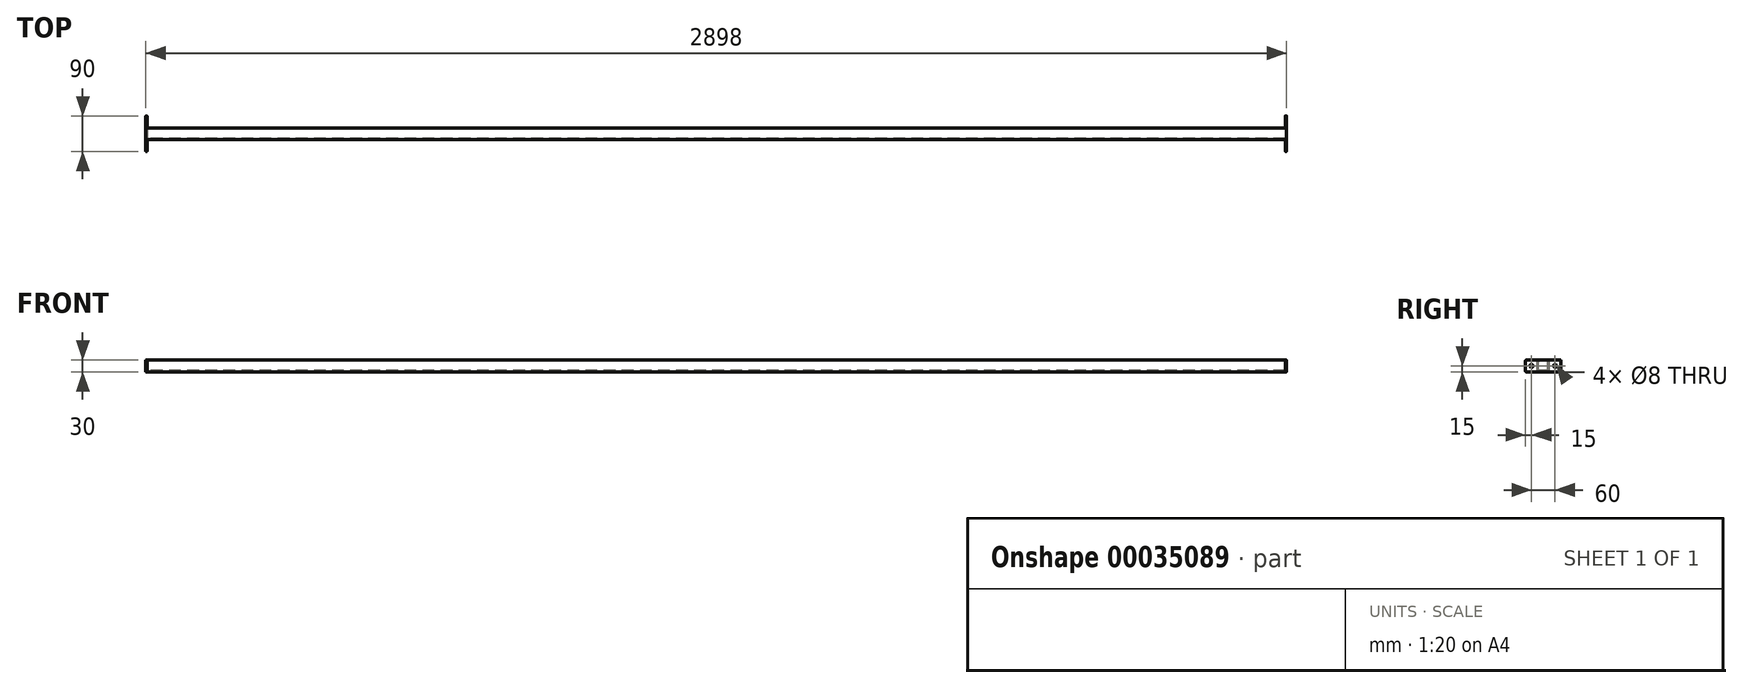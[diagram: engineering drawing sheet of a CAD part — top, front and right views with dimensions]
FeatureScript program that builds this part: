
annotation { "Feature Type Name" : "Feature", "Feature Type Description" : "" }
export const myFeature = defineFeature(function(context is Context, id is Id, definition is map)
    precondition{}
    {
        {
            var Q0;
            Q0=qCreatedBy(makeId("Right.planeOp"),FACE);
            var sketch = newSketch(context, id + "F0", { "sketchPlane" : qUnion([Q0])});
            skLineSegment(sketch, "E0.rect.bottom", {"start": v(12, -15) * mm, "end": v(-12, -15) * mm});
            skLineSegment(sketch, "E0.rect.top", {"start": v(12, 15) * mm, "end": v(-12, 15) * mm});
            skLineSegment(sketch, "E0.rect.left", {"start": v(15, -12) * mm, "end": v(15, 12) * mm});
            skLineSegment(sketch, "E0.rect.right", {"start": v(-15, -12) * mm, "end": v(-15, 12) * mm});
            skPoint(sketch, "E0.rect.middle", {"position": v(0, 0) * mm});
            skPoint(sketch, "E1.visualSharp", {"position": v(-15, 15) * mm});
            skArc(sketch, "E1.filletArc", {"start": v(-12, 15) * mm, "mid": v(-14.12, 14.12) * mm, "end": v(-15, 12) * mm});
            skPoint(sketch, "E2.visualSharp", {"position": v(15, 15) * mm});
            skArc(sketch, "E2.filletArc", {"start": v(15, 12) * mm, "mid": v(14.12, 14.12) * mm, "end": v(12, 15) * mm});
            skPoint(sketch, "E3.visualSharp", {"position": v(15, -15) * mm});
            skArc(sketch, "E3.filletArc", {"start": v(12, -15) * mm, "mid": v(14.12, -14.12) * mm, "end": v(15, -12) * mm});
            skPoint(sketch, "E4.visualSharp", {"position": v(-15, -15) * mm});
            skArc(sketch, "E4.filletArc", {"start": v(-15, -12) * mm, "mid": v(-14.12, -14.12) * mm, "end": v(-12, -15) * mm});
            skLineSegment(sketch, "E5.0", {"start": v(10, -12) * mm, "end": v(-10, -12) * mm});
            skLineSegment(sketch, "E5.1", {"start": v(12, -10) * mm, "end": v(12, 10) * mm});
            skLineSegment(sketch, "E5.2", {"start": v(10, 12) * mm, "end": v(-10, 12) * mm});
            skLineSegment(sketch, "E5.3", {"start": v(-12, -10) * mm, "end": v(-12, 10) * mm});
            skArc(sketch, "E6.filletArc", {"start": v(-10, 12) * mm, "mid": v(-11.41, 11.41) * mm, "end": v(-12, 10) * mm});
            skArc(sketch, "E7.filletArc", {"start": v(12, 10) * mm, "mid": v(11.41, 11.41) * mm, "end": v(10, 12) * mm});
            skArc(sketch, "E8.filletArc", {"start": v(10, -12) * mm, "mid": v(11.41, -11.41) * mm, "end": v(12, -10) * mm});
            skArc(sketch, "E9.filletArc", {"start": v(-12, -10) * mm, "mid": v(-11.41, -11.41) * mm, "end": v(-10, -12) * mm});
            skSolve(sketch);
        }
        {
            var Q0;
            Q0=qCreatedBy(makeId("Right.planeOp"),FACE);
            cPlane(context, id + "F1", {"entities" : qUnion([Q0]), "cplaneType" : CPlaneType.OFFSET, "offset" : 2898 * mm, "width" : 150 * mm, "height" : 150 * mm});
        }
        {
            var Q0;
            Q0=qSketchRegion(id+"F0",true);
            var Q1;
            Q1=qCreatedBy(id+"F1.planeOp",FACE);
            extrude(context, id + "F2", {"entities" : qUnion([Q0]), "endBound" : BoundingType.UP_TO_SURFACE, "endBoundEntityFace" : qUnion([Q1]), "depth" : 25 * mm});
        }
        {
            var Q0;
            Q0=qCreatedBy(makeId("Right.planeOp"),FACE);
            var sketch = newSketch(context, id + "F3", { "sketchPlane" : qUnion([Q0])});
            skLineSegment(sketch, "E10.bottom", {"start": v(43, 15) * mm, "end": v(-43, 15) * mm});
            skLineSegment(sketch, "E10.top", {"start": v(43, -15) * mm, "end": v(-43, -15) * mm});
            skLineSegment(sketch, "E10.left", {"start": v(45, 13) * mm, "end": v(45, -13) * mm});
            skLineSegment(sketch, "E10.right", {"start": v(-45, 13) * mm, "end": v(-45, -13) * mm});
            skPoint(sketch, "E11.visualSharp", {"position": v(45, 15) * mm});
            skArc(sketch, "E11.filletArc", {"start": v(45, 13) * mm, "mid": v(44.41, 14.41) * mm, "end": v(43, 15) * mm});
            skPoint(sketch, "E12.visualSharp", {"position": v(45, -15) * mm});
            skArc(sketch, "E12.filletArc", {"start": v(43, -15) * mm, "mid": v(44.41, -14.41) * mm, "end": v(45, -13) * mm});
            skPoint(sketch, "E13.visualSharp", {"position": v(-45, 15) * mm});
            skArc(sketch, "E13.filletArc", {"start": v(-43, 15) * mm, "mid": v(-44.41, 14.41) * mm, "end": v(-45, 13) * mm});
            skPoint(sketch, "E14.visualSharp", {"position": v(-45, -15) * mm});
            skArc(sketch, "E14.filletArc", {"start": v(-45, -13) * mm, "mid": v(-44.41, -14.41) * mm, "end": v(-43, -15) * mm});
            skPoint(sketch, "E15", {"position": v(30, 0) * mm});
            skPoint(sketch, "E16", {"position": v(-30, 0) * mm});
            skSolve(sketch);
        }
        {
            var Q0;
            Q0=qSketchRegion(id+"F3",true);
            extrude(context, id + "F4", {"entities" : qUnion([Q0]), "operationType" : NewBodyOperationType.ADD, "depth" : 3 * mm});
        }
        {
            var Q0;
            Q0=sQuery(id+"F3.wireOp",VERTEX,"E15");
            var Q1;
            Q1=sQuery(id+"F3.wireOp",VERTEX,"E16");
            var Q2;
            Q2=makeQuery(id+"F2.opExtrude","SWEPT_BODY",BODY,{"disambiguationData":[OSD([sQuery(id+"F0.wireOp",EDGE,"E0.rect.bottom"),sQuery(id+"F0.wireOp",EDGE,"E0.rect.top"),sQuery(id+"F0.wireOp",EDGE,"E0.rect.left"),sQuery(id+"F0.wireOp",EDGE,"E0.rect.right"),sQuery(id+"F0.wireOp",EDGE,"E1.filletArc"),sQuery(id+"F0.wireOp",EDGE,"E2.filletArc"),sQuery(id+"F0.wireOp",EDGE,"E3.filletArc"),sQuery(id+"F0.wireOp",EDGE,"E4.filletArc"),sQuery(id+"F0.wireOp",EDGE,"E5.0"),sQuery(id+"F0.wireOp",EDGE,"E5.1"),sQuery(id+"F0.wireOp",EDGE,"E5.2"),sQuery(id+"F0.wireOp",EDGE,"E5.3"),sQuery(id+"F0.wireOp",EDGE,"E6.filletArc"),sQuery(id+"F0.wireOp",EDGE,"E7.filletArc"),sQuery(id+"F0.wireOp",EDGE,"E8.filletArc"),sQuery(id+"F0.wireOp",EDGE,"E9.filletArc")])]});
            hole(context, id + "F5", {"style" : HoleStyle.SIMPLE, "holeDiameter" : 8 * mm, "endStyle" : HoleEndStyle.THROUGH, "oppositeDirection" : true, "locations" : qUnion([Q0, Q1]), "scope" : qUnion([Q2])});
        }
        {
            var Q0;
            Q0=qCreatedBy(id+"F1.planeOp",FACE);
            var sketch = newSketch(context, id + "F6", { "sketchPlane" : qUnion([Q0])});
            skLineSegment(sketch, "E17.0", {"start": v(43, 15) * mm, "end": v(-43, 15) * mm});
            skLineSegment(sketch, "E18.0", {"start": v(45, 13) * mm, "end": v(45, -13) * mm});
            skCircle(sketch, "E19.0", {"center": v(30, 0) * mm, "radius": 4 * mm});
            skCircle(sketch, "E20.0", {"center": v(-30, 0) * mm, "radius": 4 * mm});
            skLineSegment(sketch, "E21.0", {"start": v(-45, 13) * mm, "end": v(-45, -13) * mm});
            skLineSegment(sketch, "E22.0", {"start": v(43, -15) * mm, "end": v(-43, -15) * mm});
            skArc(sketch, "E23.0", {"start": v(-43, 15) * mm, "mid": v(-44.41, 14.41) * mm, "end": v(-45, 13) * mm});
            skArc(sketch, "E24.0", {"start": v(45, 13) * mm, "mid": v(44.41, 14.41) * mm, "end": v(43, 15) * mm});
            skArc(sketch, "E25.0", {"start": v(43, -15) * mm, "mid": v(44.41, -14.41) * mm, "end": v(45, -13) * mm});
            skArc(sketch, "E26.0", {"start": v(-45, -13) * mm, "mid": v(-44.41, -14.41) * mm, "end": v(-43, -15) * mm});
            skSolve(sketch);
        }
        {
            var Q0;
            Q0=qSketchRegion(id+"F6",true);
            extrude(context, id + "F7", {"entities" : qUnion([Q0]), "operationType" : NewBodyOperationType.ADD, "oppositeDirection" : true, "depth" : 3 * mm});
        }
    });
